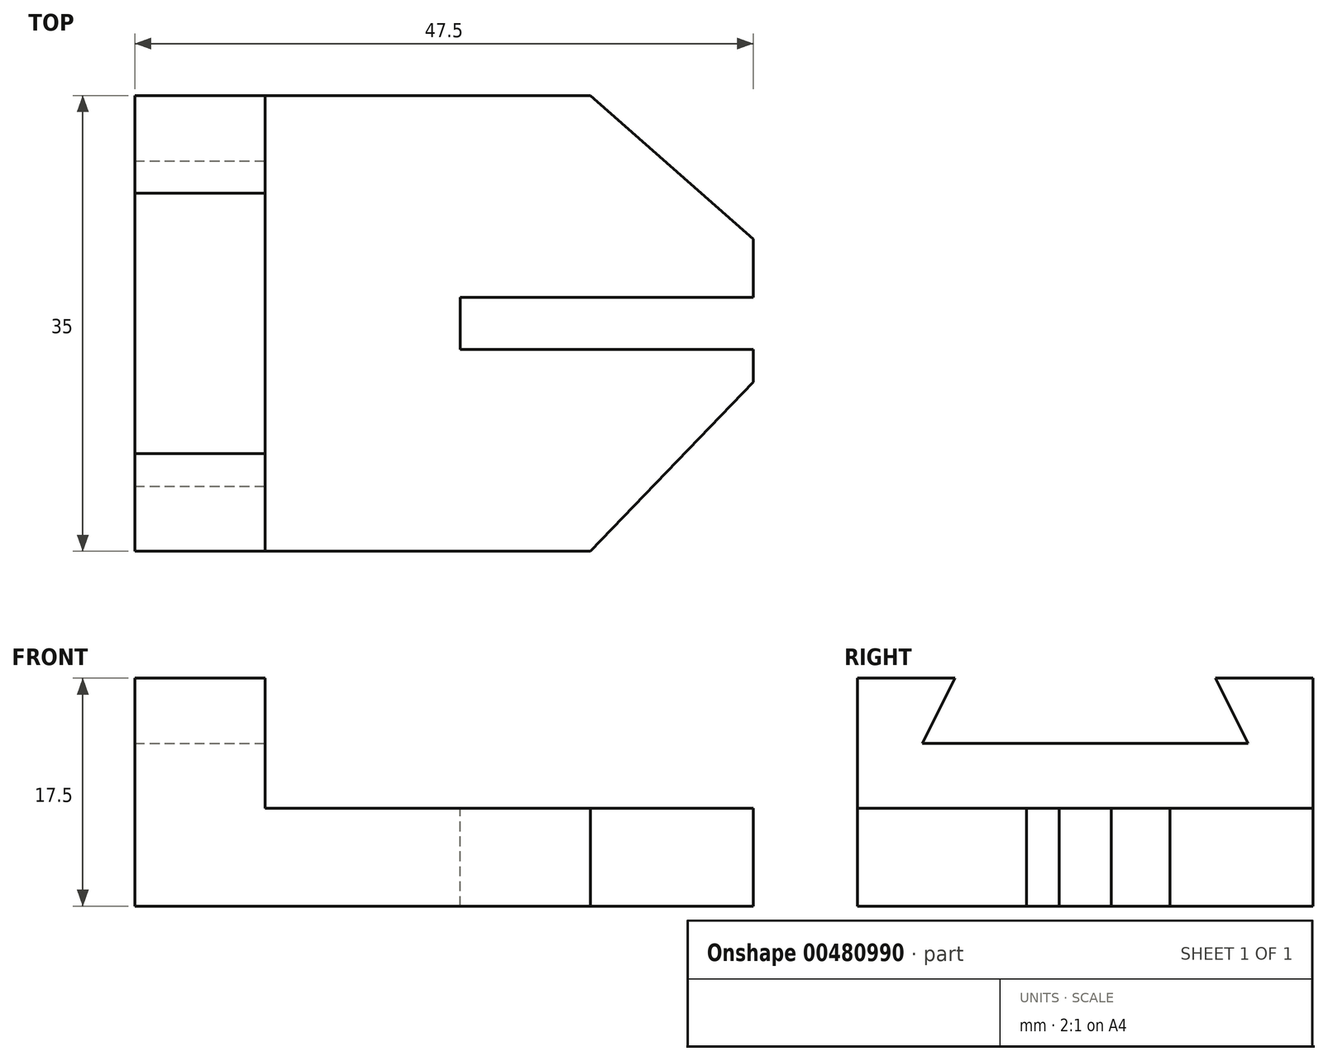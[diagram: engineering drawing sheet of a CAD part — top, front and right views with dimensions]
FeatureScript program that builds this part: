
annotation { "Feature Type Name" : "Feature", "Feature Type Description" : "" }
export const myFeature = defineFeature(function(context is Context, id is Id, definition is map)
    precondition{}
    {
        {
            var Q0;
            Q0=qCreatedBy(makeId("Top.planeOp"),FACE);
            var sketch = newSketch(context, id + "F0", { "sketchPlane" : qUnion([Q0])});
            skLineSegment(sketch, "E0.bottom", {"start": v(-15.25, 3.18) * mm, "end": v(32.25, 3.18) * mm});
            skLineSegment(sketch, "E0.top", {"start": v(-15.25, -31.82) * mm, "end": v(32.25, -31.82) * mm});
            skLineSegment(sketch, "E0.left", {"start": v(-15.25, 3.18) * mm, "end": v(-15.25, -31.82) * mm});
            skLineSegment(sketch, "E0.right", {"start": v(32.25, 3.18) * mm, "end": v(32.25, -31.82) * mm});
            skSolve(sketch);
        }
        {
            var Q0;
            Q0=makeQuery(id+"F0.imprint","IMPRINT",FACE,{"disambiguationData":[TD([[makeQuery(id+"F0.imprint","IMPRINT",EDGE,{"derivedFrom":sQuery(id+"F0.wireOp",EDGE,"E0.bottom")}),-1.0]])]});
            extrude(context, id + "F1", {"entities" : qUnion([Q0]), "depth" : 7.5 * mm});
        }
        {
            var Q0;
            Q0=makeQuery(id+"F1.opExtrude","CAP_FACE",FACE,{"disambiguationData":[OSD([sQuery(id+"F0.wireOp",EDGE,"E0.bottom"),sQuery(id+"F0.wireOp",EDGE,"E0.top"),sQuery(id+"F0.wireOp",EDGE,"E0.left"),sQuery(id+"F0.wireOp",EDGE,"E0.right")])],"isStart":false});
            var sketch = newSketch(context, id + "F2", { "sketchPlane" : qUnion([Q0])});
            skLineSegment(sketch, "E1.bottom", {"start": v(-15.25, 3.18) * mm, "end": v(-5.25, 3.18) * mm});
            skLineSegment(sketch, "E1.top", {"start": v(-15.25, -31.82) * mm, "end": v(-5.25, -31.82) * mm});
            skLineSegment(sketch, "E1.left", {"start": v(-15.25, 3.18) * mm, "end": v(-15.25, -31.82) * mm});
            skLineSegment(sketch, "E1.right", {"start": v(-5.25, 3.18) * mm, "end": v(-5.25, -31.82) * mm});
            skSolve(sketch);
        }
        {
            var Q0;
            Q0=makeQuery(id+"F2.imprint","IMPRINT",FACE,{"disambiguationData":[TD([[makeQuery(id+"F2.imprint","IMPRINT",EDGE,{"derivedFrom":sQuery(id+"F2.wireOp",EDGE,"E1.bottom")}),-1.0]])]});
            extrude(context, id + "F3", {"entities" : qUnion([Q0]), "operationType" : NewBodyOperationType.ADD, "depth" : 10 * mm});
        }
        {
            var Q0;
            Q0=makeQuery(id+"F3.opExtrude","SWEPT_FACE",FACE,{"disambiguationData":[OSD([sQuery(id+"F2.wireOp",EDGE,"E1.right")])]});
            var sketch = newSketch(context, id + "F4", { "sketchPlane" : qUnion([Q0])});
            skLineSegment(sketch, "E2", {"start": v(3.18, 17.5) * mm, "end": v(-4.32, 17.5) * mm});
            skLineSegment(sketch, "E3", {"start": v(-4.32, 17.5) * mm, "end": v(-1.82, 17.5) * mm});
            skLineSegment(sketch, "E4", {"start": v(-31.82, 17.5) * mm, "end": v(-24.32, 17.5) * mm});
            skLineSegment(sketch, "E5", {"start": v(-31.82, 17.5) * mm, "end": v(-26.82, 17.5) * mm});
            skLineSegment(sketch, "E6", {"start": v(-26.82, 12.5) * mm, "end": v(-1.82, 12.5) * mm});
            skLineSegment(sketch, "E7", {"start": v(-4.32, 17.5) * mm, "end": v(-1.82, 12.5) * mm});
            skLineSegment(sketch, "E8", {"start": v(-24.32, 17.5) * mm, "end": v(-26.82, 12.5) * mm});
            skSolve(sketch);
        }
        {
            var Q0;
            Q0=makeQuery(id+"F4.imprint","IMPRINT",FACE,{"disambiguationData":[TD([[makeQuery(id+"F4.imprint","IMPRINT",EDGE,{"derivedFrom":sQuery(id+"F4.wireOp",EDGE,"E6")}),1.0]])]});
            extrude(context, id + "F5", {"entities" : qUnion([Q0]), "operationType" : NewBodyOperationType.REMOVE, "endBound" : BoundingType.THROUGH_ALL, "oppositeDirection" : true, "depth" : 25 * mm});
        }
        {
            var Q0;
            Q0=makeQuery(id+"F1.opExtrude","CAP_FACE",FACE,{"disambiguationData":[OSD([sQuery(id+"F0.wireOp",EDGE,"E0.bottom"),sQuery(id+"F0.wireOp",EDGE,"E0.top"),sQuery(id+"F0.wireOp",EDGE,"E0.left"),sQuery(id+"F0.wireOp",EDGE,"E0.right")])],"isStart":false});
            var sketch = newSketch(context, id + "F6", { "sketchPlane" : qUnion([Q0])});
            skLineSegment(sketch, "E9", {"start": v(32.25, -31.82) * mm, "end": v(32.25, -18.82) * mm});
            skLineSegment(sketch, "E10", {"start": v(32.25, -18.82) * mm, "end": v(32.25, -16.32) * mm});
            skLineSegment(sketch, "E11", {"start": v(32.25, -16.32) * mm, "end": v(32.25, -12.32) * mm});
            skLineSegment(sketch, "E12", {"start": v(32.25, -12.32) * mm, "end": v(32.25, -9.82) * mm});
            skLineSegment(sketch, "E13", {"start": v(32.25, -31.82) * mm, "end": v(19.75, -31.82) * mm});
            skLineSegment(sketch, "E14", {"start": v(19.75, -31.82) * mm, "end": v(32.25, -18.82) * mm});
            skLineSegment(sketch, "E15", {"start": v(19.75, -31.82) * mm, "end": v(19.75, 3.18) * mm});
            skLineSegment(sketch, "E16", {"start": v(19.75, 3.18) * mm, "end": v(32.25, -9.82) * mm});
            skSolve(sketch);
        }
        {
            var Q0;
            Q0=makeQuery(id+"F6.imprint","IMPRINT",FACE,{"disambiguationData":[TD([[makeQuery(id+"F6.imprint","IMPRINT",EDGE,{"derivedFrom":sQuery(id+"F6.wireOp",EDGE,"E9")}),-1.0]])]});
            extrude(context, id + "F7", {"entities" : qUnion([Q0]), "operationType" : NewBodyOperationType.REMOVE, "endBound" : BoundingType.THROUGH_ALL, "oppositeDirection" : true, "depth" : 25 * mm});
        }
        {
            var Q0;
            Q0=makeQuery(id+"F1.opExtrude","CAP_FACE",FACE,{"disambiguationData":[OSD([sQuery(id+"F0.wireOp",EDGE,"E0.bottom"),sQuery(id+"F0.wireOp",EDGE,"E0.top"),sQuery(id+"F0.wireOp",EDGE,"E0.left"),sQuery(id+"F0.wireOp",EDGE,"E0.right")])],"isStart":false});
            var sketch = newSketch(context, id + "F8", { "sketchPlane" : qUnion([Q0])});
            skLineSegment(sketch, "E17", {"start": v(32.25, -7.82) * mm, "end": v(19.75, 3.18) * mm});
            skSolve(sketch);
        }
        {
            var Q0;
            {var subQ0=sQuery(id+"F8.wireOp",EDGE,"E17");Q0=makeQuery(id+"F8.imprint","IMPRINT",FACE,{"disambiguationData":[TD([[makeQuery(id+"F8.imprint","IMPRINT",EDGE,{"derivedFrom":subQ0}),-1.0]])]});}
            extrude(context, id + "F9", {"entities" : qUnion([Q0]), "operationType" : NewBodyOperationType.REMOVE, "endBound" : BoundingType.THROUGH_ALL, "oppositeDirection" : true, "depth" : 25 * mm});
        }
        {
            var Q0;
            Q0=makeQuery(id+"F1.opExtrude","CAP_FACE",FACE,{"disambiguationData":[OSD([sQuery(id+"F0.wireOp",EDGE,"E0.bottom"),sQuery(id+"F0.wireOp",EDGE,"E0.top"),sQuery(id+"F0.wireOp",EDGE,"E0.left"),sQuery(id+"F0.wireOp",EDGE,"E0.right")])],"isStart":false});
            var sketch = newSketch(context, id + "F10", { "sketchPlane" : qUnion([Q0])});
            skLineSegment(sketch, "E18", {"start": v(32.25, -18.82) * mm, "end": v(32.25, -16.32) * mm});
            skLineSegment(sketch, "E19", {"start": v(32.25, -16.32) * mm, "end": v(32.25, -12.32) * mm});
            skLineSegment(sketch, "E20.bottom", {"start": v(32.25, -16.32) * mm, "end": v(9.75, -16.32) * mm});
            skLineSegment(sketch, "E20.top", {"start": v(32.25, -12.32) * mm, "end": v(9.75, -12.32) * mm});
            skLineSegment(sketch, "E20.right", {"start": v(9.75, -16.32) * mm, "end": v(9.75, -12.32) * mm});
            skSolve(sketch);
        }
        {
            var Q0;
            Q0=makeQuery(id+"F10.imprint","IMPRINT",FACE,{"disambiguationData":[TD([[makeQuery(id+"F10.imprint","IMPRINT",EDGE,{"derivedFrom":sQuery(id+"F10.wireOp",EDGE,"E20.bottom")}),-1.0]])]});
            extrude(context, id + "F11", {"entities" : qUnion([Q0]), "operationType" : NewBodyOperationType.REMOVE, "endBound" : BoundingType.THROUGH_ALL, "oppositeDirection" : true, "depth" : 25 * mm});
        }
    });
